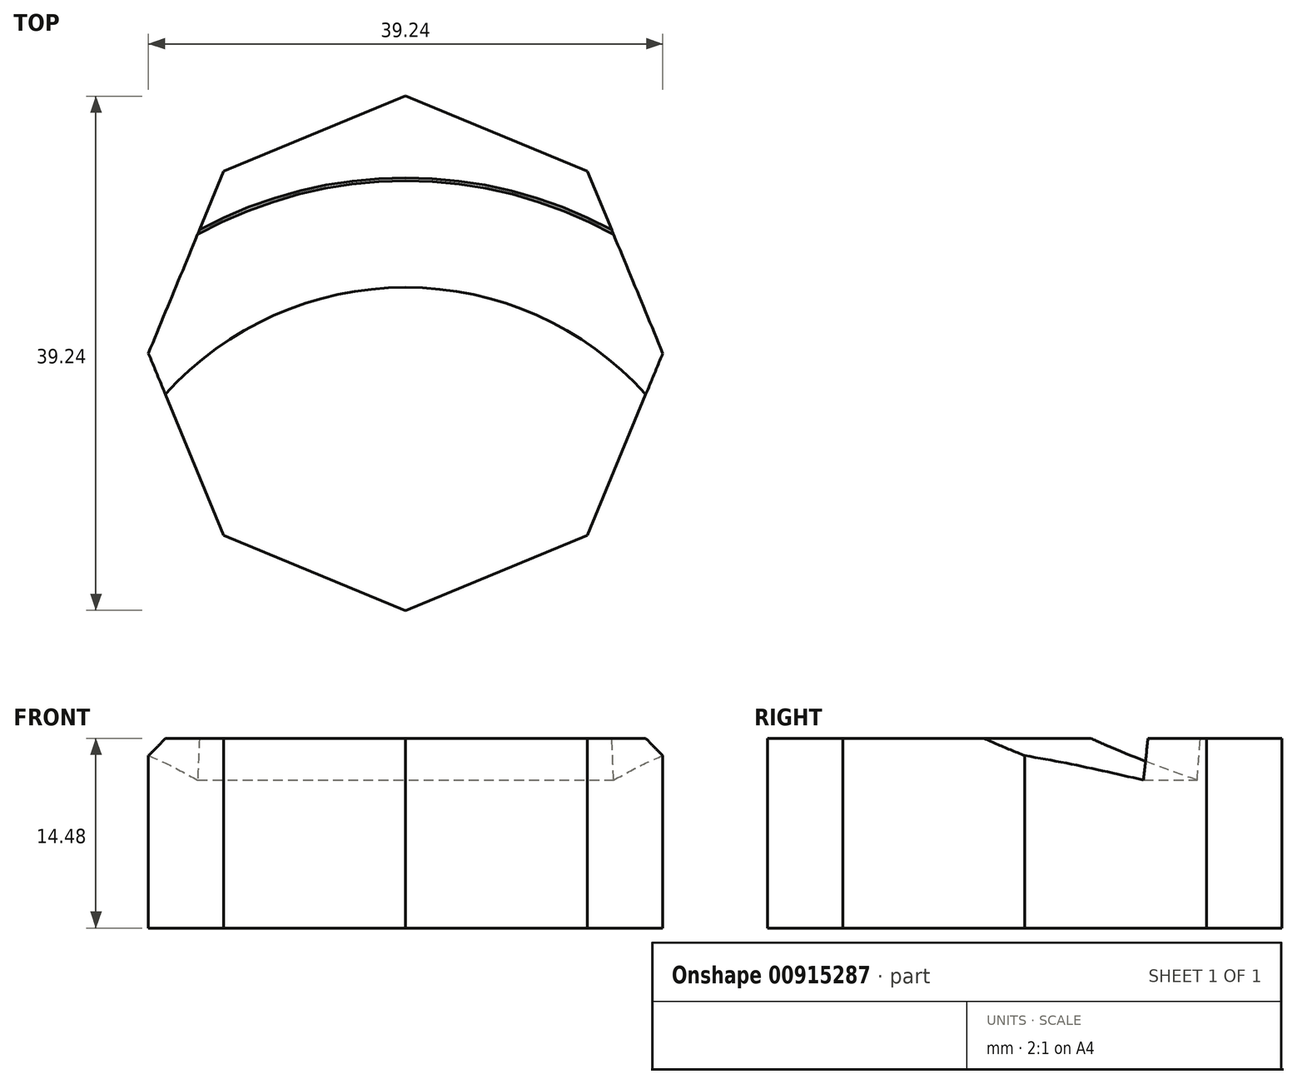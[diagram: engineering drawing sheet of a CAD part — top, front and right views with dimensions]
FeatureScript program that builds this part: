
annotation { "Feature Type Name" : "Feature", "Feature Type Description" : "" }
export const myFeature = defineFeature(function(context is Context, id is Id, definition is map)
    precondition{}
    {
        {
            var Q0;
            Q0=qCreatedBy(makeId("Top.planeOp"),FACE);
            var sketch = newSketch(context, id + "F0", { "sketchPlane" : qUnion([Q0])});
            skCircle(sketch, "E0.cCircle", {"center": v(0, 0) * mm, "radius": 18.13 * mm, "construction": true});
            skLineSegment(sketch, "E0.0", {"start": v(19.62, 0) * mm, "end": v(13.88, -13.88) * mm});
            skLineSegment(sketch, "E0.1", {"start": v(13.88, -13.88) * mm, "end": v(0, -19.62) * mm});
            skLineSegment(sketch, "E0.2", {"start": v(0, -19.62) * mm, "end": v(-13.88, -13.88) * mm});
            skLineSegment(sketch, "E0.3", {"start": v(-13.88, -13.88) * mm, "end": v(-19.62, 0) * mm});
            skLineSegment(sketch, "E0.4", {"start": v(-19.62, 0) * mm, "end": v(-13.88, 13.88) * mm});
            skLineSegment(sketch, "E0.5", {"start": v(-13.88, 13.88) * mm, "end": v(0, 19.62) * mm});
            skLineSegment(sketch, "E0.6", {"start": v(0, 19.62) * mm, "end": v(13.88, 13.88) * mm});
            skLineSegment(sketch, "E0.7", {"start": v(13.88, 13.88) * mm, "end": v(19.62, 0) * mm});
            skPoint(sketch, "E0.0.midPoint", {"position": v(16.75, -6.94) * mm});
            skCircle(sketch, "E1", {"center": v(0, 0) * mm, "radius": 11.25 * mm});
            skSolve(sketch);
        }
        {
            var Q0;
            Q0 = qSketchRegion(id + "F0", true);
            var Q1;
            Q1=makeQuery(id+"F0.imprint","IMPRINT",FACE,{"disambiguationData":[TD([[makeQuery(id+"F0.imprint","IMPRINT",EDGE,{"derivedFrom":sQuery(id+"F0.wireOp",EDGE,"E1")}),1.0]])]});
            extrude(context, id + "F1", {"entities" : qUnion([Q0, Q1]), "depth" : 14.48 * mm, "offsetDistance" : 25.4 * mm});
        }
        {
            var Q0;
            Q0=qCreatedBy(makeId("Front.planeOp"),FACE);
            var sketch = newSketch(context, id + "F2", { "sketchPlane" : qUnion([Q0])});
            skLineSegment(sketch, "E2", {"start": v(26.56, 14.64) * mm, "end": v(19.6, 14.64) * mm});
            skLineSegment(sketch, "E3", {"start": v(26.26, 11.28) * mm, "end": v(26.56, 14.64) * mm});
            skLineSegment(sketch, "E4", {"start": v(19.6, 0) * mm, "end": v(26.26, 0) * mm});
            skLineSegment(sketch, "E5", {"start": v(26.26, 0) * mm, "end": v(26.26, 3.65) * mm});
            skLineSegment(sketch, "E6", {"start": v(26.26, 3.65) * mm, "end": v(19.6, 0) * mm});
            skLineSegment(sketch, "E7", {"start": v(26.56, 14.64) * mm, "end": v(14.34, 14.64) * mm});
            skLineSegment(sketch, "E8", {"start": v(26.26, 11.28) * mm, "end": v(14.34, 14.64) * mm});
            skSolve(sketch);
        }
        {
            var Q0;
            {var subQ0=sQuery(id+"F2.wireOp",EDGE,"E3");Q0=makeQuery(id+"F2.imprint","IMPRINT",FACE,{"disambiguationData":[TD([[makeQuery(id+"F2.imprint","IMPRINT",EDGE,{"derivedFrom":subQ0}),1.0]])]});}
            var Q1;
            Q1=makeQuery(id+"F1.opExtrude","SWEPT_EDGE",EDGE,{"disambiguationData":[OSD([sQuery(id+"F0.wireOp",EDGE,"E0.1"),sQuery(id+"F0.wireOp",EDGE,"E0.2")])]});
            revolve(context, id + "F3", {"operationType" : NewBodyOperationType.REMOVE, "surfaceOperationType" : NewSurfaceOperationType.NEW, "entities" : qUnion([Q0]), "axis" : qUnion([Q1]), "revolveType" : RevolveType.FULL, "oppositeDirection" : true});
        }
    });
